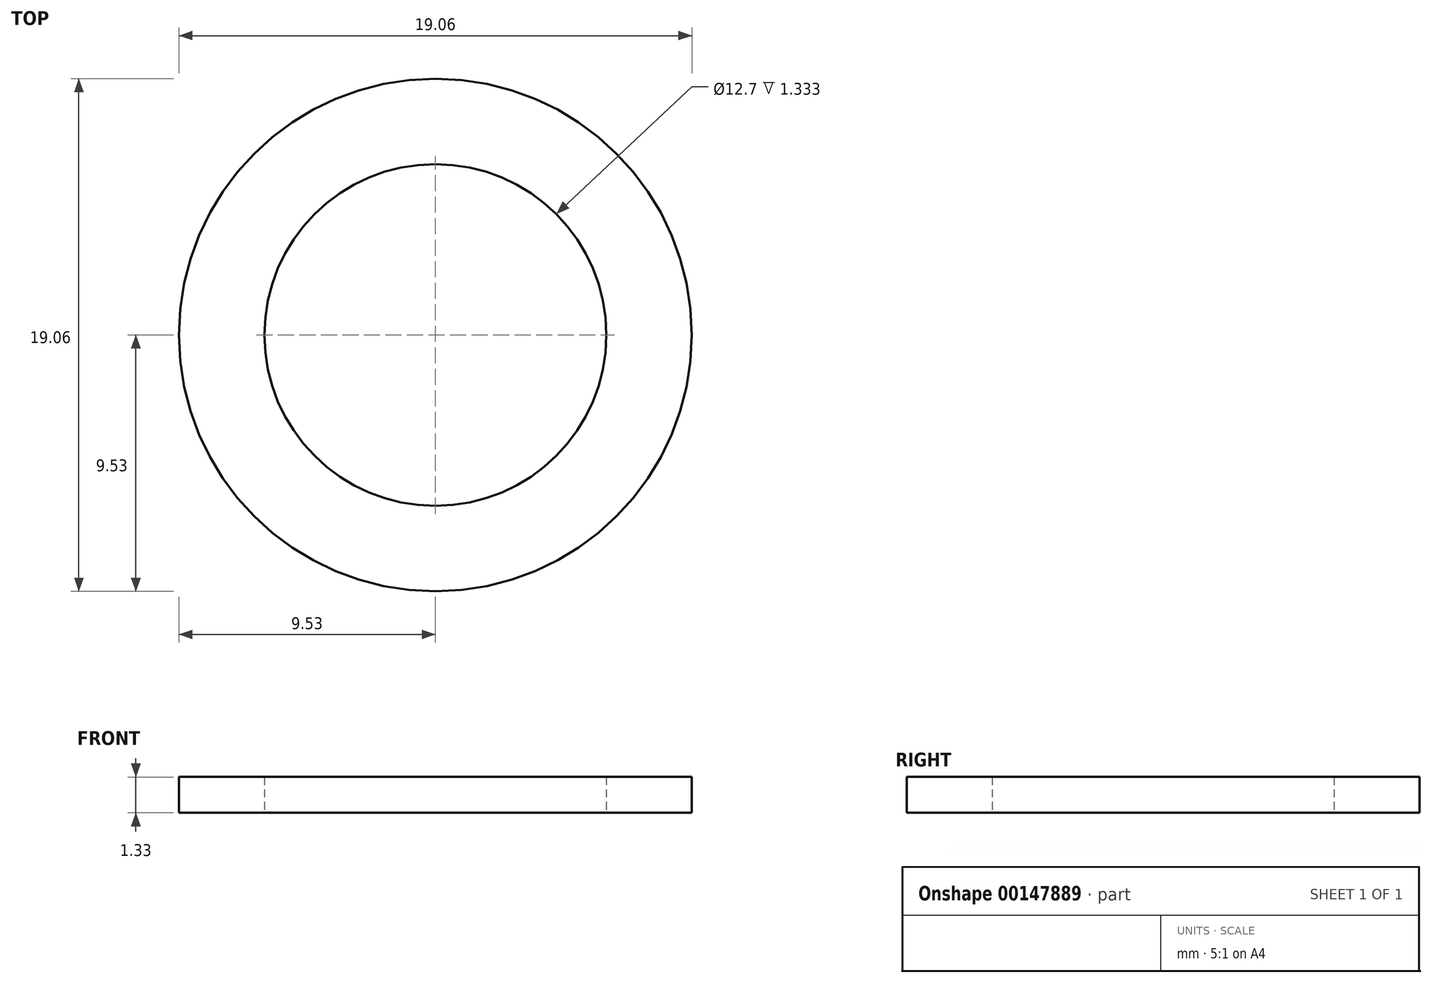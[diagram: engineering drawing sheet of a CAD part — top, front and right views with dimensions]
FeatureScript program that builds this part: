
annotation { "Feature Type Name" : "Feature", "Feature Type Description" : "" }
export const myFeature = defineFeature(function(context is Context, id is Id, definition is map)
    precondition{}
    {
        {
            var Q0;
            Q0=qCreatedBy(makeId("Top.planeOp"),FACE);
            var sketch = newSketch(context, id + "F0", { "sketchPlane" : qUnion([Q0])});
            skCircle(sketch, "E0", {"center": v(0, 0) * mm, "radius": 6.35 * mm});
            skCircle(sketch, "E1", {"center": v(0, 0) * mm, "radius": 9.53 * mm});
            skSolve(sketch);
        }
        {
            var Q0;
            Q0=qSketchRegion(id+"F0",true);
            extrude(context, id + "F1", {"entities" : qUnion([Q0]), "depth" : 1.33 * mm});
        }
    });
